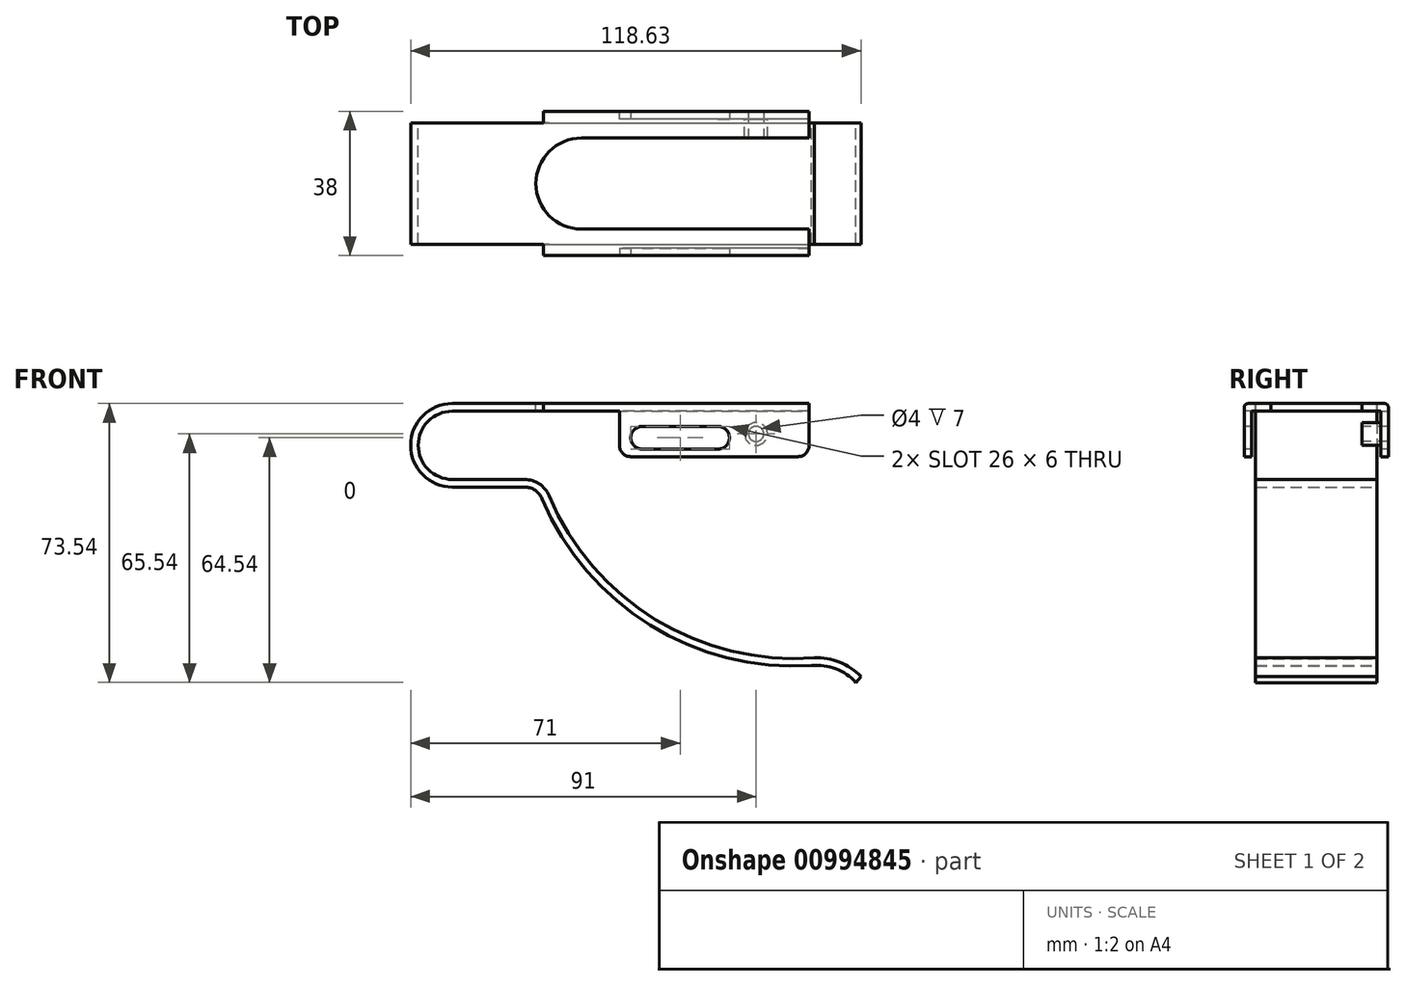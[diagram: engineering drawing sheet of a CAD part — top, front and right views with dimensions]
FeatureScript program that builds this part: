
annotation { "Feature Type Name" : "Feature", "Feature Type Description" : "" }
export const myFeature = defineFeature(function(context is Context, id is Id, definition is map)
    precondition{}
    {
        {
            var Q0;
            Q0=qCreatedBy(makeId("Front.planeOp"),FACE);
            var sketch = newSketch(context, id + "F0", { "sketchPlane" : qUnion([Q0])});
            skArc(sketch, "E0", {"start": v(0, 11) * mm, "mid": v(-11, 0) * mm, "end": v(0, -11) * mm});
            skLineSegment(sketch, "E1", {"start": v(0, 11) * mm, "end": v(94, 11) * mm});
            skLineSegment(sketch, "E2", {"start": v(0, -11) * mm, "end": v(19, -11) * mm});
            skArc(sketch, "E3", {"start": v(23.61, -14.06) * mm, "mid": v(52.09, -47.41) * mm, "end": v(94.63, -58.05) * mm});
            skArc(sketch, "E4", {"start": v(106.34, -62.54) * mm, "mid": v(101.02, -58.91) * mm, "end": v(94.63, -58.05) * mm});
            skPoint(sketch, "E5.visualSharp", {"position": v(22.4, -11) * mm});
            skArc(sketch, "E5.filletArc", {"start": v(23.61, -14.06) * mm, "mid": v(21.77, -11.84) * mm, "end": v(19, -11) * mm});
            skLineSegment(sketch, "E6.0", {"start": v(0, 9) * mm, "end": v(94, 9) * mm});
            skArc(sketch, "E6.1", {"start": v(0, 9) * mm, "mid": v(-9, 0) * mm, "end": v(0, -9) * mm});
            skArc(sketch, "E6.2", {"start": v(107.63, -61) * mm, "mid": v(102, -57.16) * mm, "end": v(95.3, -56) * mm});
            skArc(sketch, "E6.3", {"start": v(25.45, -13.3) * mm, "mid": v(53.48, -45.92) * mm, "end": v(95.3, -56) * mm});
            skArc(sketch, "E6.4", {"start": v(25.45, -13.3) * mm, "mid": v(22.88, -10.17) * mm, "end": v(19, -9) * mm});
            skLineSegment(sketch, "E6.5", {"start": v(0, -9) * mm, "end": v(19, -9) * mm});
            skLineSegment(sketch, "E7", {"start": v(94, 11) * mm, "end": v(94, 9) * mm});
            skLineSegment(sketch, "E8", {"start": v(107.63, -61) * mm, "end": v(106.34, -62.54) * mm});
            skSolve(sketch);
        }
        {
            var Q0;
            Q0=makeQuery(id+"F0.imprint","IMPRINT",FACE,{"disambiguationData":[TD([[makeQuery(id+"F0.imprint","IMPRINT",EDGE,{"derivedFrom":sQuery(id+"F0.wireOp",EDGE,"E0")}),1.0]])]});
            extrude(context, id + "F1", {"entities" : qUnion([Q0]), "depth" : 16 * mm, "offsetDistance" : 25 * mm});
        }
        {
            var Q0;
            Q0=makeQuery(id+"F1.opExtrude","SWEPT_FACE",FACE,{"disambiguationData":[OSD([sQuery(id+"F0.wireOp",EDGE,"E1")])]});
            var sketch = newSketch(context, id + "F2", { "sketchPlane" : qUnion([Q0])});
            skLineSegment(sketch, "E9.bottom", {"start": v(94, -16) * mm, "end": v(24, -16) * mm});
            skLineSegment(sketch, "E9.top", {"start": v(94, -19) * mm, "end": v(24, -19) * mm});
            skLineSegment(sketch, "E9.left", {"start": v(94, -16) * mm, "end": v(94, -19) * mm});
            skLineSegment(sketch, "E9.right", {"start": v(24, -16) * mm, "end": v(24, -19) * mm});
            skSolve(sketch);
        }
        {
            var Q0;
            Q0=makeQuery(id+"F2.imprint","IMPRINT",FACE,{"disambiguationData":[TD([[makeQuery(id+"F2.imprint","IMPRINT",EDGE,{"derivedFrom":sQuery(id+"F2.wireOp",EDGE,"E9.bottom")}),-1.0]])]});
            extrude(context, id + "F3", {"entities" : qUnion([Q0]), "operationType" : NewBodyOperationType.ADD, "oppositeDirection" : true, "depth" : 2 * mm, "offsetDistance" : 25 * mm});
        }
        {
            var Q0;
            Q0=makeQuery(id+"F3.opExtrude","SWEPT_FACE",FACE,{"disambiguationData":[OSD([sQuery(id+"F2.wireOp",EDGE,"E9.top")])]});
            var sketch = newSketch(context, id + "F4", { "sketchPlane" : qUnion([Q0])});
            skLineSegment(sketch, "E10.bottom", {"start": v(94, 11) * mm, "end": v(44, 11) * mm});
            skLineSegment(sketch, "E10.top", {"start": v(94, -3) * mm, "end": v(44, -3) * mm});
            skLineSegment(sketch, "E10.left", {"start": v(94, 11) * mm, "end": v(94, -3) * mm});
            skLineSegment(sketch, "E10.right", {"start": v(44, 11) * mm, "end": v(44, -3) * mm});
            skSolve(sketch);
        }
        {
            var Q0;
            {var subQ0=sQuery(id+"F4.wireOp",EDGE,"E10.top");Q0=makeQuery(id+"F4.imprint","IMPRINT",FACE,{"disambiguationData":[TD([[makeQuery(id+"F4.imprint","IMPRINT",EDGE,{"derivedFrom":subQ0}),-1.0]])]});}
            extrude(context, id + "F5", {"entities" : qUnion([Q0]), "operationType" : NewBodyOperationType.ADD, "oppositeDirection" : true, "depth" : 2 * mm, "offsetDistance" : 25 * mm});
        }
        {
            var Q0;
            Q0=makeQuery(id+"F3.opExtrude","CAP_EDGE",EDGE,{"disambiguationData":[OSD([sQuery(id+"F2.wireOp",EDGE,"E9.top")])],"isStart":true});
            var Q1;
            Q1=makeQuery(id+"F5.opExtrude","CAP_EDGE",EDGE,{"disambiguationData":[OSD([sQuery(id+"F2.wireOp",EDGE,"E9.top")])],"isStart":false});
            fillet(context, id + "F6", {"entities" : qUnion([Q0, Q1]), "radius" : 1 * mm, "allowEdgeOverflow" : false});
        }
        {
            var Q0;
            Q0=makeQuery(id+"F1.opExtrude","SWEPT_BODY",BODY,{"disambiguationData":[OSD([sQuery(id+"F0.wireOp",EDGE,"E0"),sQuery(id+"F0.wireOp",EDGE,"E1"),sQuery(id+"F0.wireOp",EDGE,"E2"),sQuery(id+"F0.wireOp",EDGE,"E3"),sQuery(id+"F0.wireOp",EDGE,"E4"),sQuery(id+"F0.wireOp",EDGE,"E5.filletArc"),sQuery(id+"F0.wireOp",EDGE,"E6.0"),sQuery(id+"F0.wireOp",EDGE,"E6.1"),sQuery(id+"F0.wireOp",EDGE,"E6.2"),sQuery(id+"F0.wireOp",EDGE,"E6.3"),sQuery(id+"F0.wireOp",EDGE,"E6.4"),sQuery(id+"F0.wireOp",EDGE,"E6.5"),sQuery(id+"F0.wireOp",EDGE,"E7"),sQuery(id+"F0.wireOp",EDGE,"E8")])]});
            var Q1;
            Q1=qCreatedBy(makeId("Front.planeOp"),FACE);
            mirror(context, id + "F7", {"operationType" : NewBodyOperationType.ADD, "entities" : qUnion([Q0]), "mirrorPlane" : qUnion([Q1])});
        }
        {
            var Q0;
            {var subQ0=makeQuery(id+"F3.boolean.opBoolean","MERGE",FACE,{"derivedFrom":[makeQuery(id+"F1.opExtrude","SWEPT_FACE",FACE,{"disambiguationData":[OSD([sQuery(id+"F0.wireOp",EDGE,"E1")])]}),makeQuery(id+"F3.opExtrude","CAP_FACE",FACE,{"disambiguationData":[OSD([sQuery(id+"F2.wireOp",EDGE,"E9.bottom"),sQuery(id+"F2.wireOp",EDGE,"E9.top"),sQuery(id+"F2.wireOp",EDGE,"E9.left"),sQuery(id+"F2.wireOp",EDGE,"E9.right")])],"isStart":true})]});Q0=makeQuery(id+"F7.boolean.opBoolean","MERGE",FACE,{"derivedFrom":[subQ0,makeQuery(id+"F7.opPattern","COPY",FACE,{"derivedFrom":subQ0,"instanceName":"1"})]});}
            var sketch = newSketch(context, id + "F8", { "sketchPlane" : qUnion([Q0])});
            skArc(sketch, "E11", {"start": v(34, 12) * mm, "mid": v(22, 0) * mm, "end": v(34, -12) * mm});
            skLineSegment(sketch, "E12", {"start": v(34, -12) * mm, "end": v(94, -12) * mm});
            skLineSegment(sketch, "E13", {"start": v(94, -12) * mm, "end": v(94, 12) * mm});
            skLineSegment(sketch, "E14", {"start": v(94, 12) * mm, "end": v(34, 12) * mm});
            skSolve(sketch);
        }
        {
            var Q0;
            Q0=makeQuery(id+"F8.imprint","IMPRINT",FACE,{"disambiguationData":[TD([[makeQuery(id+"F8.imprint","IMPRINT",EDGE,{"derivedFrom":sQuery(id+"F8.wireOp",EDGE,"E11")}),1.0]])]});
            extrude(context, id + "F9", {"entities" : qUnion([Q0]), "operationType" : NewBodyOperationType.REMOVE, "oppositeDirection" : true, "depth" : 2 * mm, "offsetDistance" : 25 * mm});
        }
        {
            var Q0;
            {var subQ0=sQuery(id+"F2.wireOp",EDGE,"E9.top");Q0=makeQuery(id+"F5.boolean.opBoolean","MERGE",FACE,{"derivedFrom":[makeQuery(id+"F3.opExtrude","SWEPT_FACE",FACE,{"disambiguationData":[OSD([subQ0])]}),makeQuery(id+"F5.opExtrude","CAP_FACE",FACE,{"disambiguationData":[OSD([subQ0,sQuery(id+"F4.wireOp",EDGE,"E10.top"),sQuery(id+"F4.wireOp",EDGE,"E10.left"),sQuery(id+"F4.wireOp",EDGE,"E10.right")])],"isStart":true})]});}
            var sketch = newSketch(context, id + "F10", { "sketchPlane" : qUnion([Q0])});
            skLineSegment(sketch, "E15", {"start": v(50, 2) * mm, "end": v(70, 2) * mm});
            skArc(sketch, "E16.0.startCap", {"start": v(50, -1) * mm, "mid": v(47, 2) * mm, "end": v(50, 5) * mm});
            skArc(sketch, "E16.0.endCap", {"start": v(70, 5) * mm, "mid": v(73, 2) * mm, "end": v(70, -1) * mm});
            skLineSegment(sketch, "E16.0.left", {"start": v(50, 5) * mm, "end": v(70, 5) * mm});
            skLineSegment(sketch, "E16.0.right", {"start": v(50, -1) * mm, "end": v(70, -1) * mm});
            skSolve(sketch);
        }
        {
            var Q0;
            Q0=qSketchRegion(id+"F10",true);
            extrude(context, id + "F11", {"entities" : qUnion([Q0]), "operationType" : NewBodyOperationType.REMOVE, "endBound" : BoundingType.THROUGH_ALL, "oppositeDirection" : true, "depth" : 25 * mm, "offsetDistance" : 25 * mm});
        }
        {
            var Q0;
            Q0=qCreatedBy(makeId("Front.planeOp"),FACE);
            var sketch = newSketch(context, id + "F12", { "sketchPlane" : qUnion([Q0])});
            skPoint(sketch, "E17", {"position": v(80, 3) * mm});
            skSolve(sketch);
        }
        {
            var Q0;
            Q0=sQuery(id+"F12.wireOp",VERTEX,"E17");
            var Q1;
            Q1=makeQuery(id+"F1.opExtrude","SWEPT_BODY",BODY,{"disambiguationData":[OSD([sQuery(id+"F0.wireOp",EDGE,"E0"),sQuery(id+"F0.wireOp",EDGE,"E1"),sQuery(id+"F0.wireOp",EDGE,"E2"),sQuery(id+"F0.wireOp",EDGE,"E3"),sQuery(id+"F0.wireOp",EDGE,"E4"),sQuery(id+"F0.wireOp",EDGE,"E5.filletArc"),sQuery(id+"F0.wireOp",EDGE,"E6.0"),sQuery(id+"F0.wireOp",EDGE,"E6.1"),sQuery(id+"F0.wireOp",EDGE,"E6.2"),sQuery(id+"F0.wireOp",EDGE,"E6.3"),sQuery(id+"F0.wireOp",EDGE,"E6.4"),sQuery(id+"F0.wireOp",EDGE,"E6.5"),sQuery(id+"F0.wireOp",EDGE,"E7"),sQuery(id+"F0.wireOp",EDGE,"E8")])]});
            hole(context, id + "F13", {"style" : HoleStyle.SIMPLE, "endStyle" : HoleEndStyle.THROUGH, "holeDiameter" : 4 * mm, "majorDiameter" : 5 * mm, "isTappedThrough" : true, "tappedDepth" : 12 * mm, "tapClearance" : 3, "locations" : qUnion([Q0]), "scope" : qUnion([Q1])});
        }
        {
            var Q0;
            Q0=makeQuery(id+"F7.opPattern","COPY",FACE,{"derivedFrom":makeQuery(id+"F5.opExtrude","CAP_FACE",FACE,{"disambiguationData":[OSD([sQuery(id+"F2.wireOp",EDGE,"E9.top"),sQuery(id+"F4.wireOp",EDGE,"E10.top"),sQuery(id+"F4.wireOp",EDGE,"E10.left"),sQuery(id+"F4.wireOp",EDGE,"E10.right")])],"isStart":false}),"instanceName":"1"});
            var sketch = newSketch(context, id + "F14", { "sketchPlane" : qUnion([Q0])});
            skCircle(sketch, "E18.0", {"center": v(80, 3) * mm, "radius": 2 * mm});
            skCircle(sketch, "E19.0", {"center": v(80, 3) * mm, "radius": 3 * mm});
            skSolve(sketch);
        }
        {
            var Q0;
            Q0=makeQuery(id+"F14.imprint","IMPRINT",FACE,{"disambiguationData":[TD([[makeQuery(id+"F14.imprint","IMPRINT",EDGE,{"derivedFrom":sQuery(id+"F14.wireOp",EDGE,"E18.0")}),-1.0]])]});
            extrude(context, id + "F15", {"entities" : qUnion([Q0]), "operationType" : NewBodyOperationType.ADD, "depth" : 5 * mm, "offsetDistance" : 25 * mm});
        }
        {
            var Q0;
            Q0=makeQuery(id+"F5.opExtrude","SWEPT_EDGE",EDGE,{"disambiguationData":[OSD([sQuery(id+"F4.wireOp",EDGE,"E10.top"),sQuery(id+"F4.wireOp",EDGE,"E10.left")])]});
            var Q1;
            Q1=makeQuery(id+"F7.opPattern","COPY",EDGE,{"derivedFrom":makeQuery(id+"F5.opExtrude","SWEPT_EDGE",EDGE,{"disambiguationData":[OSD([sQuery(id+"F4.wireOp",EDGE,"E10.top"),sQuery(id+"F4.wireOp",EDGE,"E10.left")])]}),"instanceName":"1"});
            var Q2;
            Q2=makeQuery(id+"F5.opExtrude","SWEPT_EDGE",EDGE,{"disambiguationData":[OSD([sQuery(id+"F4.wireOp",EDGE,"E10.top"),sQuery(id+"F4.wireOp",EDGE,"E10.right")])]});
            var Q3;
            Q3=makeQuery(id+"F7.opPattern","COPY",EDGE,{"derivedFrom":makeQuery(id+"F5.opExtrude","SWEPT_EDGE",EDGE,{"disambiguationData":[OSD([sQuery(id+"F4.wireOp",EDGE,"E10.top"),sQuery(id+"F4.wireOp",EDGE,"E10.right")])]}),"instanceName":"1"});
            fillet(context, id + "F16", {"entities" : qUnion([Q0, Q1, Q2, Q3]), "radius" : 3 * mm, "tangentPropagation" : true, "allowEdgeOverflow" : false});
        }
    });
